annotation { "Feature Type Name" : "Feature", "Feature Type Description" : "" }
export const myFeature = defineFeature(function(context is Context, id is Id, definition is map)
    precondition{}
    {
        {
            var Q0;
            Q0=qCreatedBy(makeId("Top.planeOp"),FACE);
            var sketch = newSketch(context, id + "F0", { "sketchPlane" : qUnion([Q0])});
            skLineSegment(sketch, "E0.rect.bottom", {"start": v(-78.5, 40.5) * mm, "end": v(78.5, 40.5) * mm});
            skLineSegment(sketch, "E0.rect.top", {"start": v(-78.5, -40.5) * mm, "end": v(78.5, -40.5) * mm});
            skLineSegment(sketch, "E0.rect.left", {"start": v(-78.5, 40.5) * mm, "end": v(-78.5, -40.5) * mm});
            skLineSegment(sketch, "E0.rect.right", {"start": v(78.5, 40.5) * mm, "end": v(78.5, -40.5) * mm});
            skPoint(sketch, "E0.rect.middle", {"position": v(0, 0) * mm});
            skLineSegment(sketch, "E1.left", {"start": v(-73.5, 35.5) * mm, "end": v(-73.5, 2.5) * mm});
            skLineSegment(sketch, "E1.bottom", {"start": v(-73.5, 35.5) * mm, "end": v(-40.5, 35.5) * mm});
            skLineSegment(sketch, "E1.right", {"start": v(-40.5, 35.5) * mm, "end": v(-40.5, 2.5) * mm});
            skLineSegment(sketch, "E1.top", {"start": v(-73.5, 2.5) * mm, "end": v(-40.5, 2.5) * mm});
            skLineSegment(sketch, "E2.left", {"start": v(-35.5, 35.5) * mm, "end": v(-35.5, 2.5) * mm});
            skLineSegment(sketch, "E2.bottom", {"start": v(-35.5, 35.5) * mm, "end": v(-2.5, 35.5) * mm});
            skLineSegment(sketch, "E2.right", {"start": v(-2.5, 35.5) * mm, "end": v(-2.5, 2.5) * mm});
            skLineSegment(sketch, "E2.top", {"start": v(-35.5, 2.5) * mm, "end": v(-2.5, 2.5) * mm});
            skLineSegment(sketch, "E3.left", {"start": v(2.5, 35.5) * mm, "end": v(2.5, 2.5) * mm});
            skLineSegment(sketch, "E3.bottom", {"start": v(2.5, 35.5) * mm, "end": v(35.5, 35.5) * mm});
            skLineSegment(sketch, "E3.right", {"start": v(35.5, 35.5) * mm, "end": v(35.5, 2.5) * mm});
            skLineSegment(sketch, "E3.top", {"start": v(2.5, 2.5) * mm, "end": v(35.5, 2.5) * mm});
            skLineSegment(sketch, "E4.left", {"start": v(40.5, 35.5) * mm, "end": v(40.5, 2.5) * mm});
            skLineSegment(sketch, "E4.bottom", {"start": v(40.5, 35.5) * mm, "end": v(73.5, 35.5) * mm});
            skLineSegment(sketch, "E4.right", {"start": v(73.5, 35.5) * mm, "end": v(73.5, 2.5) * mm});
            skLineSegment(sketch, "E4.top", {"start": v(40.5, 2.5) * mm, "end": v(73.5, 2.5) * mm});
            skLineSegment(sketch, "E5.left", {"start": v(40.5, -2.5) * mm, "end": v(40.5, -35.5) * mm});
            skLineSegment(sketch, "E5.bottom", {"start": v(40.5, -2.5) * mm, "end": v(73.5, -2.5) * mm});
            skLineSegment(sketch, "E5.right", {"start": v(73.5, -2.5) * mm, "end": v(73.5, -35.5) * mm});
            skLineSegment(sketch, "E5.top", {"start": v(40.5, -35.5) * mm, "end": v(73.5, -35.5) * mm});
            skLineSegment(sketch, "E6.left", {"start": v(2.5, -2.5) * mm, "end": v(2.5, -35.5) * mm});
            skLineSegment(sketch, "E6.bottom", {"start": v(2.5, -2.5) * mm, "end": v(35.5, -2.5) * mm});
            skLineSegment(sketch, "E6.right", {"start": v(35.5, -2.5) * mm, "end": v(35.5, -35.5) * mm});
            skLineSegment(sketch, "E6.top", {"start": v(2.5, -35.5) * mm, "end": v(35.5, -35.5) * mm});
            skLineSegment(sketch, "E7.left", {"start": v(-35.5, -2.5) * mm, "end": v(-35.5, -35.5) * mm});
            skLineSegment(sketch, "E7.bottom", {"start": v(-35.5, -2.5) * mm, "end": v(-2.5, -2.5) * mm});
            skLineSegment(sketch, "E7.right", {"start": v(-2.5, -2.5) * mm, "end": v(-2.5, -35.5) * mm});
            skLineSegment(sketch, "E7.top", {"start": v(-35.5, -35.5) * mm, "end": v(-2.5, -35.5) * mm});
            skLineSegment(sketch, "E8.left", {"start": v(-73.5, -2.5) * mm, "end": v(-73.5, -35.5) * mm});
            skLineSegment(sketch, "E8.bottom", {"start": v(-73.5, -2.5) * mm, "end": v(-40.5, -2.5) * mm});
            skLineSegment(sketch, "E8.right", {"start": v(-40.5, -2.5) * mm, "end": v(-40.5, -35.5) * mm});
            skLineSegment(sketch, "E8.top", {"start": v(-73.5, -35.5) * mm, "end": v(-40.5, -35.5) * mm});
            skLineSegment(sketch, "E9.top", {"start": v(-78.5, -50.5) * mm, "end": v(78.5, -50.5) * mm});
            skLineSegment(sketch, "E9.left", {"start": v(-78.5, -40.5) * mm, "end": v(-78.5, -50.5) * mm});
            skLineSegment(sketch, "E9.right", {"start": v(78.5, -40.5) * mm, "end": v(78.5, -50.5) * mm});
            skSolve(sketch);
        }
        {
            var Q0;
            Q0=makeQuery(id+"F0.imprint","IMPRINT",FACE,{"disambiguationData":[TD([[makeQuery(id+"F0.imprint","IMPRINT",EDGE,{"derivedFrom":sQuery(id+"F0.wireOp",EDGE,"E0.rect.bottom")}),-1.0]])]});
            extrude(context, id + "F1", {"entities" : qUnion([Q0]), "depth" : 5 * mm});
        }
        {
            var Q0;
            Q0=makeQuery(id+"F0.imprint","IMPRINT",FACE,{"disambiguationData":[TD([[makeQuery(id+"F0.imprint","IMPRINT",EDGE,{"derivedFrom":sQuery(id+"F0.wireOp",EDGE,"E6.left")}),1.0]])]});
            var Q1;
            Q1=makeQuery(id+"F0.imprint","IMPRINT",FACE,{"disambiguationData":[TD([[makeQuery(id+"F0.imprint","IMPRINT",EDGE,{"derivedFrom":sQuery(id+"F0.wireOp",EDGE,"E5.left")}),1.0]])]});
            var Q2;
            Q2=makeQuery(id+"F0.imprint","IMPRINT",FACE,{"disambiguationData":[TD([[makeQuery(id+"F0.imprint","IMPRINT",EDGE,{"derivedFrom":sQuery(id+"F0.wireOp",EDGE,"E4.left")}),1.0]])]});
            var Q3;
            Q3=makeQuery(id+"F0.imprint","IMPRINT",FACE,{"disambiguationData":[TD([[makeQuery(id+"F0.imprint","IMPRINT",EDGE,{"derivedFrom":sQuery(id+"F0.wireOp",EDGE,"E3.left")}),1.0]])]});
            var Q4;
            Q4=makeQuery(id+"F0.imprint","IMPRINT",FACE,{"disambiguationData":[TD([[makeQuery(id+"F0.imprint","IMPRINT",EDGE,{"derivedFrom":sQuery(id+"F0.wireOp",EDGE,"E2.left")}),1.0]])]});
            var Q5;
            Q5=makeQuery(id+"F0.imprint","IMPRINT",FACE,{"disambiguationData":[TD([[makeQuery(id+"F0.imprint","IMPRINT",EDGE,{"derivedFrom":sQuery(id+"F0.wireOp",EDGE,"E1.left")}),1.0]])]});
            var Q6;
            Q6=makeQuery(id+"F0.imprint","IMPRINT",FACE,{"disambiguationData":[TD([[makeQuery(id+"F0.imprint","IMPRINT",EDGE,{"derivedFrom":sQuery(id+"F0.wireOp",EDGE,"E8.left")}),1.0]])]});
            var Q7;
            Q7=makeQuery(id+"F0.imprint","IMPRINT",FACE,{"disambiguationData":[TD([[makeQuery(id+"F0.imprint","IMPRINT",EDGE,{"derivedFrom":sQuery(id+"F0.wireOp",EDGE,"E7.left")}),1.0]])]});
            extrude(context, id + "F2", {"entities" : qUnion([Q0, Q1, Q2, Q3, Q4, Q5, Q6, Q7]), "operationType" : NewBodyOperationType.ADD, "depth" : 2.5 * mm});
        }
        {
            var Q0;
            Q0=makeQuery(id+"F0.imprint","IMPRINT",FACE,{"disambiguationData":[TD([[makeQuery(id+"F0.imprint","IMPRINT",EDGE,{"derivedFrom":sQuery(id+"F0.wireOp",EDGE,"E0.rect.top")}),-1.0]])]});
            extrude(context, id + "F3", {"entities" : qUnion([Q0]), "operationType" : NewBodyOperationType.ADD, "depth" : 10 * mm});
        }
        {
            var Q0;
            Q0=makeQuery(id+"F3.opExtrude","CAP_FACE",FACE,{"disambiguationData":[OSD([sQuery(id+"F0.wireOp",EDGE,"E0.rect.top"),sQuery(id+"F0.wireOp",EDGE,"E9.top"),sQuery(id+"F0.wireOp",EDGE,"E9.left"),sQuery(id+"F0.wireOp",EDGE,"E9.right")])],"isStart":false});
            var sketch = newSketch(context, id + "F4", { "sketchPlane" : qUnion([Q0])});
            skText(sketch, "E10", { "text": "Coin Rack", "fontName": "OpenSans-Regular.ttf"});
            const initialGuessF4  = {"E10": [-0.022, -0.049, 1, 0, 0.007]};
            skSetInitialGuess(sketch, initialGuessF4);
            skSolve(sketch);
        }
        {
            var Q0;
            Q0 = qSketchRegion(id + "F4", true);
            extrude(context, id + "F5", {"entities" : qUnion([Q0]), "operationType" : NewBodyOperationType.REMOVE, "oppositeDirection" : true, "depth" : 2 * mm});
        }
    });